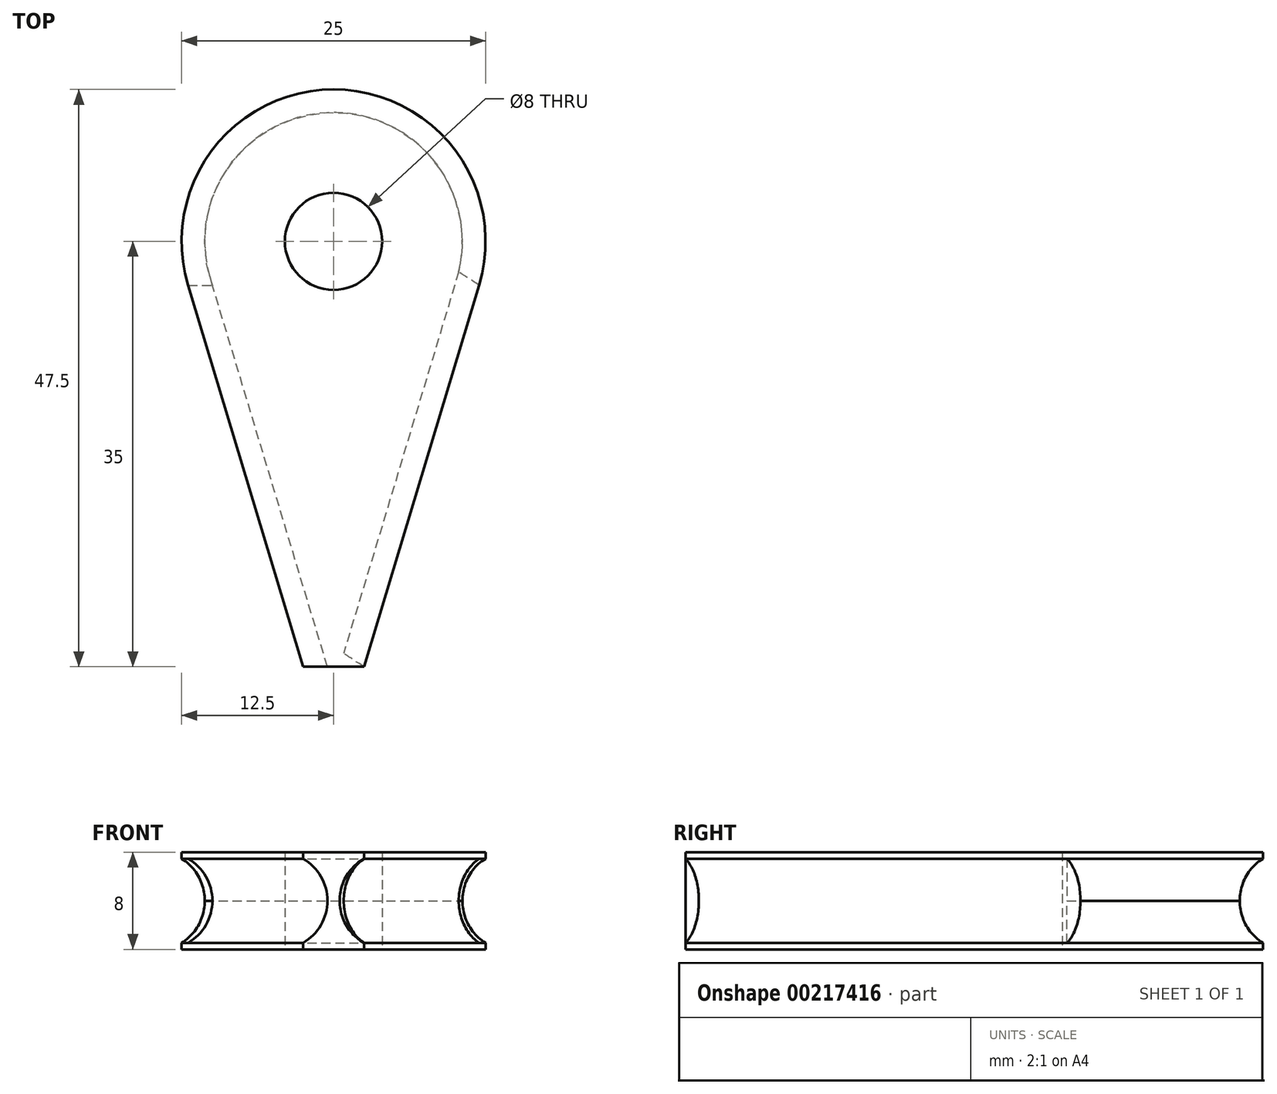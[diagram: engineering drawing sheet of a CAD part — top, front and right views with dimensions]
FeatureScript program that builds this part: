
annotation { "Feature Type Name" : "Feature", "Feature Type Description" : "" }
export const myFeature = defineFeature(function(context is Context, id is Id, definition is map)
    precondition{}
    {
        {
            var Q0;
            Q0=qCreatedBy(makeId("Top.planeOp"),FACE);
            var sketch = newSketch(context, id + "F0", { "sketchPlane" : qUnion([Q0])});
            skCircle(sketch, "E0", {"center": v(0, 0) * mm, "radius": 4 * mm});
            skArc(sketch, "E1", {"start": v(11.97, -3.6) * mm, "mid": v(0, 12.5) * mm, "end": v(-11.97, -3.6) * mm});
            skLineSegment(sketch, "E2", {"start": v(-11.97, -3.6) * mm, "end": v(-2.5, -35) * mm});
            skLineSegment(sketch, "E3", {"start": v(-2.5, -35) * mm, "end": v(2.5, -35) * mm});
            skLineSegment(sketch, "E4", {"start": v(2.5, -35) * mm, "end": v(11.97, -3.6) * mm});
            skSolve(sketch);
        }
        {
            var Q0;
            Q0=makeQuery(id+"F0.imprint","IMPRINT",FACE,{"disambiguationData":[TD([[makeQuery(id+"F0.imprint","IMPRINT",EDGE,{"derivedFrom":sQuery(id+"F0.wireOp",EDGE,"E0")}),-1.0]])]});
            extrude(context, id + "F1", {"entities" : qUnion([Q0]), "depth" : 4 * mm});
        }
        {
            var Q0;
            Q0=makeQuery(id+"F1.opExtrude","CAP_FACE",FACE,{"disambiguationData":[OSD([sQuery(id+"F0.wireOp",EDGE,"E0"),sQuery(id+"F0.wireOp",EDGE,"E1"),sQuery(id+"F0.wireOp",EDGE,"E2"),sQuery(id+"F0.wireOp",EDGE,"E3"),sQuery(id+"F0.wireOp",EDGE,"E4")])],"isStart":false});
            var sketch = newSketch(context, id + "F2", { "sketchPlane" : qUnion([Q0])});
            skLineSegment(sketch, "E5", {"start": v(2.5, -35) * mm, "end": v(0.34, -42.16) * mm});
            skSolve(sketch);
        }
        {
            var Q0;
            Q0=makeQuery(id+"F1.opExtrude","SWEPT_FACE",FACE,{"disambiguationData":[OSD([sQuery(id+"F0.wireOp",EDGE,"E3")])]});
            var sketch = newSketch(context, id + "F3", { "sketchPlane" : qUnion([Q0])});
            skCircle(sketch, "E6", {"center": v(-4.5, 4) * mm, "radius": 4 * mm});
            skSolve(sketch);
        }
        {
            var Q0;
            {var subQ0=sQuery(id+"F3.wireOp",EDGE,"E6");var subQ1=sQuery(id+"F0.wireOp",EDGE,"E3");var subQ4=makeQuery(id+"F1.opExtrude","CAP_EDGE",EDGE,{"disambiguationData":[OSD([subQ1])],"isStart":false});var subQ5=makeQuery(id+"F3.imprint","INTERSECT",VERTEX,{"derivedFrom":[subQ4,subQ0]});Q0=makeQuery(id+"F3.imprint","IMPRINT",FACE,{"disambiguationData":[TD([[makeQuery(id+"F3.imprint","IMPRINT",EDGE,{"disambiguationData":[TD([[subQ5,1.0]])],"derivedFrom":subQ0}),1.0]])]});}
            var Q1;
            Q1=sQuery(id+"F3.wireOp",EDGE,"E6");
            var Q2;
            Q2=makeQuery(id+"F1.opExtrude","CAP_EDGE",EDGE,{"disambiguationData":[OSD([sQuery(id+"F0.wireOp",EDGE,"E2")])],"isStart":false});
            var Q3;
            Q3=makeQuery(id+"F1.opExtrude","CAP_EDGE",EDGE,{"disambiguationData":[OSD([sQuery(id+"F0.wireOp",EDGE,"E1")])],"isStart":false});
            var Q4;
            Q4=makeQuery(id+"F1.opExtrude","CAP_EDGE",EDGE,{"disambiguationData":[OSD([sQuery(id+"F0.wireOp",EDGE,"E4")])],"isStart":false});
            var Q5;
            Q5=sQuery(id+"F2.wireOp",EDGE,"E5");
            sweep(context, id + "F4", {"operationType" : NewBodyOperationType.REMOVE, "profiles" : qUnion([Q0]), "surfaceProfiles" : qUnion([Q1]), "path" : qUnion([Q2, Q3, Q4, Q5])});
        }
        {
            var Q0;
            Q0=makeQuery(id+"F1.opExtrude","SWEPT_BODY",BODY,{"disambiguationData":[OSD([sQuery(id+"F0.wireOp",EDGE,"E0"),sQuery(id+"F0.wireOp",EDGE,"E1"),sQuery(id+"F0.wireOp",EDGE,"E2"),sQuery(id+"F0.wireOp",EDGE,"E3"),sQuery(id+"F0.wireOp",EDGE,"E4")])]});
            var Q1;
            Q1=makeQuery(id+"F1.opExtrude","CAP_FACE",FACE,{"disambiguationData":[OSD([sQuery(id+"F0.wireOp",EDGE,"E0"),sQuery(id+"F0.wireOp",EDGE,"E1"),sQuery(id+"F0.wireOp",EDGE,"E2"),sQuery(id+"F0.wireOp",EDGE,"E3"),sQuery(id+"F0.wireOp",EDGE,"E4")])],"isStart":false});
            mirror(context, id + "F5", {"operationType" : NewBodyOperationType.ADD, "entities" : qUnion([Q0]), "mirrorPlane" : qUnion([Q1])});
        }
    });
